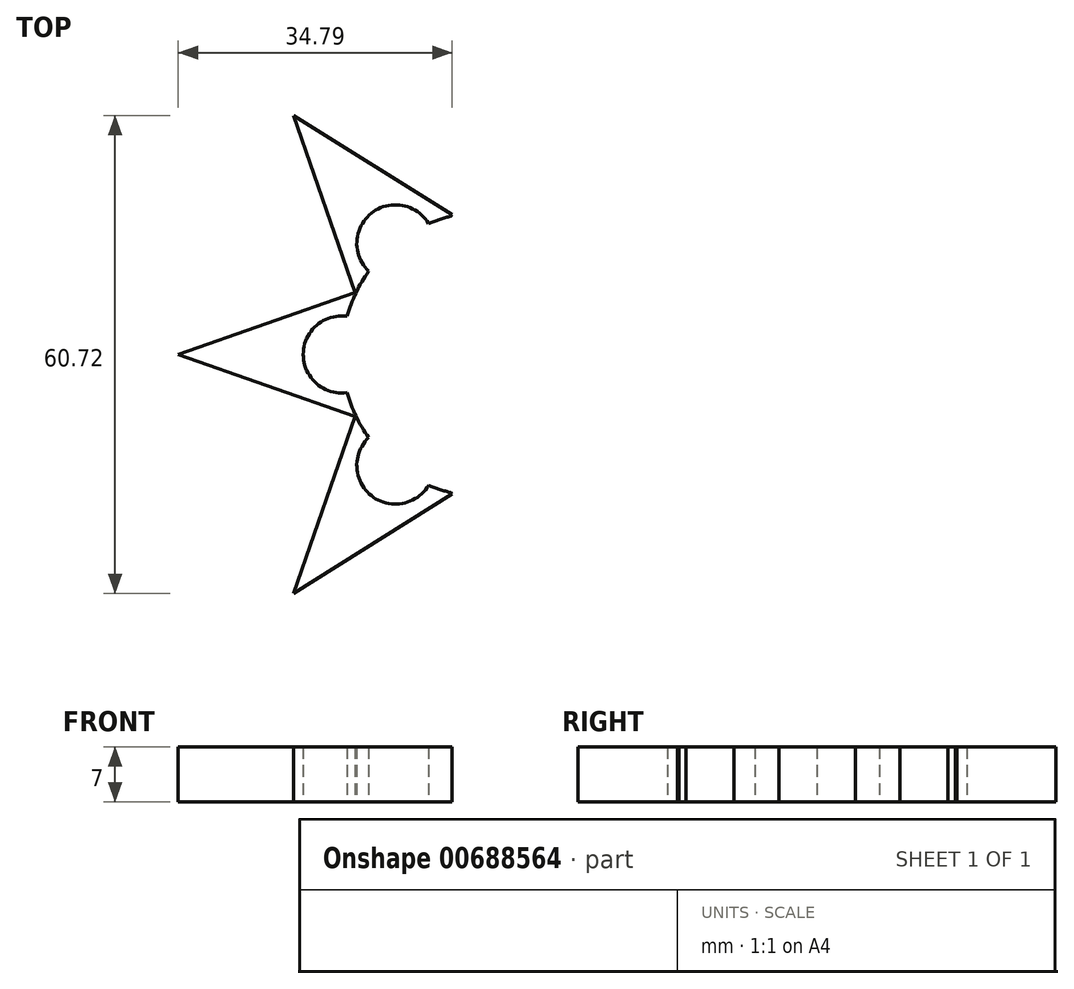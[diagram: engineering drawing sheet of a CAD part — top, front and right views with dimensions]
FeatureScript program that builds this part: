
annotation { "Feature Type Name" : "Feature", "Feature Type Description" : "" }
export const myFeature = defineFeature(function(context is Context, id is Id, definition is map)
    precondition{}
    {
        {
            var Q0;
            Q0=qCreatedBy(makeId("Top.planeOp"),FACE);
            var sketch = newSketch(context, id + "F0", { "sketchPlane" : qUnion([Q0])});
            skCircle(sketch, "E0", {"center": v(0, 0) * mm, "radius": 11.15 * mm});
            skCircle(sketch, "E1", {"center": v(0, 0) * mm, "radius": 18.05 * mm});
            skLineSegment(sketch, "E2", {"start": v(-16.2, 7.97) * mm, "end": v(-38.84, 0) * mm});
            skLineSegment(sketch, "E3.MirrorCS", {"start": v(-16.2, -7.97) * mm, "end": v(-38.84, 0) * mm});
            skLineSegment(sketch, "E4.1.0", {"start": v(-16.33, -7.7) * mm, "end": v(-24.21, -30.36) * mm});
            skLineSegment(sketch, "E4.1.1", {"start": v(-3.87, -17.63) * mm, "end": v(-24.21, -30.36) * mm});
            skLineSegment(sketch, "E4.2.0", {"start": v(-4.16, -17.56) * mm, "end": v(8.64, -37.86) * mm});
            skLineSegment(sketch, "E4.2.1", {"start": v(11.37, -14.02) * mm, "end": v(8.64, -37.86) * mm});
            skLineSegment(sketch, "E4.3.0", {"start": v(11.14, -14.2) * mm, "end": v(34.99, -16.85) * mm});
            skLineSegment(sketch, "E4.3.1", {"start": v(18.05, 0.15) * mm, "end": v(34.99, -16.85) * mm});
            skLineSegment(sketch, "E4.4.0", {"start": v(18.05, -0.15) * mm, "end": v(34.99, 16.85) * mm});
            skLineSegment(sketch, "E4.4.1", {"start": v(11.14, 14.2) * mm, "end": v(34.99, 16.85) * mm});
            skLineSegment(sketch, "E4.5.0", {"start": v(11.37, 14.02) * mm, "end": v(8.64, 37.86) * mm});
            skLineSegment(sketch, "E4.5.1", {"start": v(-4.16, 17.56) * mm, "end": v(8.64, 37.86) * mm});
            skLineSegment(sketch, "E4.6.0", {"start": v(-3.87, 17.63) * mm, "end": v(-24.21, 30.36) * mm});
            skLineSegment(sketch, "E4.6.1", {"start": v(-16.33, 7.7) * mm, "end": v(-24.21, 30.36) * mm});
            skCircle(sketch, "E5", {"center": v(-18.05, 0) * mm, "radius": 4.9 * mm});
            skCircle(sketch, "E6.1.0", {"center": v(-11.25, -14.11) * mm, "radius": 4.9 * mm});
            skCircle(sketch, "E6.2.0", {"center": v(4.02, -17.6) * mm, "radius": 4.9 * mm});
            skCircle(sketch, "E6.3.0", {"center": v(16.26, -7.83) * mm, "radius": 4.9 * mm});
            skCircle(sketch, "E6.4.0", {"center": v(16.26, 7.83) * mm, "radius": 4.9 * mm});
            skCircle(sketch, "E6.5.0", {"center": v(4.02, 17.6) * mm, "radius": 4.9 * mm});
            skCircle(sketch, "E6.6.0", {"center": v(-11.25, 14.11) * mm, "radius": 4.9 * mm});
            skSolve(sketch);
        }
        {
            var Q0;
            Q0=makeQuery(id+"F0.imprint","IMPRINT",FACE,{"disambiguationData":[TD([[makeQuery(id+"F0.imprint","IMPRINT",EDGE,{"derivedFrom":sQuery(id+"F0.wireOp",EDGE,"E0")}),1.0]])]});
            var Q1;
            {var subQ1=sQuery(id+"F0.wireOp",EDGE,"E1");var subQ5=sQuery(id+"F0.wireOp",EDGE,"E4.6.0");var subQ6=makeQuery(id+"F0.imprint","INTERSECT",VERTEX,{"derivedFrom":[subQ1,subQ5]});Q1=makeQuery(id+"F0.imprint","IMPRINT",FACE,{"disambiguationData":[TD([[makeQuery(id+"F0.imprint","IMPRINT",EDGE,{"disambiguationData":[TD([[subQ6,-1.0]])],"derivedFrom":subQ1}),1.0]])]});}
            var Q2;
            {var subQ8=sQuery(id+"F0.wireOp",EDGE,"E3.MirrorCS");var subQ9=sQuery(id+"F0.wireOp",EDGE,"E2");var subQ10=makeQuery(id+"F0.imprint","INTERSECT",VERTEX,{"derivedFrom":[subQ9,subQ8]});Q2=makeQuery(id+"F0.imprint","IMPRINT",FACE,{"disambiguationData":[TD([[makeQuery(id+"F0.imprint","IMPRINT",EDGE,{"disambiguationData":[TD([[subQ10,1.0]])],"derivedFrom":subQ9}),1.0]])]});}
            var Q3;
            {var subQ1=sQuery(id+"F0.wireOp",EDGE,"E1");var subQ8=sQuery(id+"F0.wireOp",EDGE,"E2");var subQ11=makeQuery(id+"F0.imprint","INTERSECT",VERTEX,{"derivedFrom":[subQ8,subQ1]});Q3=makeQuery(id+"F0.imprint","IMPRINT",FACE,{"disambiguationData":[TD([[makeQuery(id+"F0.imprint","IMPRINT",EDGE,{"disambiguationData":[TD([[subQ11,-1.0]])],"derivedFrom":subQ8}),-1.0]])]});}
            var Q4;
            {var subQ1=sQuery(id+"F0.wireOp",EDGE,"E1");var subQ10=sQuery(id+"F0.wireOp",EDGE,"E4.5.0");var subQ11=makeQuery(id+"F0.imprint","INTERSECT",VERTEX,{"derivedFrom":[subQ1,subQ10]});Q4=makeQuery(id+"F0.imprint","IMPRINT",FACE,{"disambiguationData":[TD([[makeQuery(id+"F0.imprint","IMPRINT",EDGE,{"disambiguationData":[TD([[subQ11,-1.0]])],"derivedFrom":subQ1}),1.0]])]});}
            var Q5;
            {var subQ1=sQuery(id+"F0.wireOp",EDGE,"E1");var subQ9=sQuery(id+"F0.wireOp",EDGE,"E4.4.0");var subQ10=makeQuery(id+"F0.imprint","INTERSECT",VERTEX,{"derivedFrom":[subQ1,subQ9]});Q5=makeQuery(id+"F0.imprint","IMPRINT",FACE,{"disambiguationData":[TD([[makeQuery(id+"F0.imprint","IMPRINT",EDGE,{"disambiguationData":[TD([[subQ10,-1.0]])],"derivedFrom":subQ1}),1.0]])]});}
            var Q6;
            {var subQ0=sQuery(id+"F0.wireOp",EDGE,"E1");var subQ1=sQuery(id+"F0.wireOp",EDGE,"E3.MirrorCS");var subQ2=makeQuery(id+"F0.imprint","INTERSECT",VERTEX,{"derivedFrom":[subQ1,subQ0]});Q6=makeQuery(id+"F0.imprint","IMPRINT",FACE,{"disambiguationData":[TD([[makeQuery(id+"F0.imprint","IMPRINT",EDGE,{"disambiguationData":[TD([[subQ2,-1.0]])],"derivedFrom":subQ1}),-1.0]])]});}
            var Q7;
            {var subQ0=sQuery(id+"F0.wireOp",EDGE,"E1");var subQ1=sQuery(id+"F0.wireOp",EDGE,"E2");var subQ2=makeQuery(id+"F0.imprint","INTERSECT",VERTEX,{"derivedFrom":[subQ1,subQ0]});Q7=makeQuery(id+"F0.imprint","IMPRINT",FACE,{"disambiguationData":[TD([[makeQuery(id+"F0.imprint","IMPRINT",EDGE,{"disambiguationData":[TD([[subQ2,-1.0]])],"derivedFrom":subQ1}),1.0]])]});}
            var Q8;
            {var subQ0=sQuery(id+"F0.wireOp",EDGE,"E4.5.1");var subQ1=sQuery(id+"F0.wireOp",EDGE,"E1");var subQ2=makeQuery(id+"F0.imprint","INTERSECT",VERTEX,{"derivedFrom":[subQ1,subQ0]});Q8=makeQuery(id+"F0.imprint","IMPRINT",FACE,{"disambiguationData":[TD([[makeQuery(id+"F0.imprint","IMPRINT",EDGE,{"disambiguationData":[TD([[subQ2,-1.0]])],"derivedFrom":subQ1}),1.0]])]});}
            var Q9;
            {var subQ0=sQuery(id+"F0.wireOp",EDGE,"E4.3.1");var subQ1=sQuery(id+"F0.wireOp",EDGE,"E1");var subQ2=makeQuery(id+"F0.imprint","INTERSECT",VERTEX,{"derivedFrom":[subQ1,subQ0]});Q9=makeQuery(id+"F0.imprint","IMPRINT",FACE,{"disambiguationData":[TD([[makeQuery(id+"F0.imprint","IMPRINT",EDGE,{"disambiguationData":[TD([[subQ2,-1.0]])],"derivedFrom":subQ1}),1.0]])]});}
            var Q10;
            {var subQ0=sQuery(id+"F0.wireOp",EDGE,"E4.4.1");var subQ1=sQuery(id+"F0.wireOp",EDGE,"E1");var subQ2=makeQuery(id+"F0.imprint","INTERSECT",VERTEX,{"derivedFrom":[subQ1,subQ0]});Q10=makeQuery(id+"F0.imprint","IMPRINT",FACE,{"disambiguationData":[TD([[makeQuery(id+"F0.imprint","IMPRINT",EDGE,{"disambiguationData":[TD([[subQ2,-1.0]])],"derivedFrom":subQ1}),1.0]])]});}
            var Q11;
            {var subQ0=sQuery(id+"F0.wireOp",EDGE,"E4.2.1");var subQ1=sQuery(id+"F0.wireOp",EDGE,"E1");var subQ2=makeQuery(id+"F0.imprint","INTERSECT",VERTEX,{"derivedFrom":[subQ1,subQ0]});Q11=makeQuery(id+"F0.imprint","IMPRINT",FACE,{"disambiguationData":[TD([[makeQuery(id+"F0.imprint","IMPRINT",EDGE,{"disambiguationData":[TD([[subQ2,-1.0]])],"derivedFrom":subQ1}),1.0]])]});}
            var Q12;
            {var subQ0=sQuery(id+"F0.wireOp",EDGE,"E4.1.1");var subQ1=sQuery(id+"F0.wireOp",EDGE,"E1");var subQ2=makeQuery(id+"F0.imprint","INTERSECT",VERTEX,{"derivedFrom":[subQ1,subQ0]});Q12=makeQuery(id+"F0.imprint","IMPRINT",FACE,{"disambiguationData":[TD([[makeQuery(id+"F0.imprint","IMPRINT",EDGE,{"disambiguationData":[TD([[subQ2,-1.0]])],"derivedFrom":subQ1}),1.0]])]});}
            var Q13;
            {var subQ5=sQuery(id+"F0.wireOp",EDGE,"E1");var subQ9=sQuery(id+"F0.wireOp",EDGE,"E4.3.0");var subQ10=makeQuery(id+"F0.imprint","INTERSECT",VERTEX,{"derivedFrom":[subQ5,subQ9]});Q13=makeQuery(id+"F0.imprint","IMPRINT",FACE,{"disambiguationData":[TD([[makeQuery(id+"F0.imprint","IMPRINT",EDGE,{"disambiguationData":[TD([[subQ10,-1.0]])],"derivedFrom":subQ5}),1.0]])]});}
            var Q14;
            {var subQ3=sQuery(id+"F0.wireOp",EDGE,"E3.MirrorCS");var subQ5=sQuery(id+"F0.wireOp",EDGE,"E1");var subQ6=makeQuery(id+"F0.imprint","INTERSECT",VERTEX,{"derivedFrom":[subQ3,subQ5]});Q14=makeQuery(id+"F0.imprint","IMPRINT",FACE,{"disambiguationData":[TD([[makeQuery(id+"F0.imprint","IMPRINT",EDGE,{"disambiguationData":[TD([[subQ6,-1.0]])],"derivedFrom":subQ3}),1.0]])]});}
            extrude(context, id + "F1", {"entities" : qUnion([Q0, Q1, Q2, Q3, Q4, Q5, Q6, Q7, Q8, Q9, Q10, Q11, Q12, Q13, Q14]), "depth" : 7 * mm, "offsetDistance" : 25 * mm});
        }
    });
